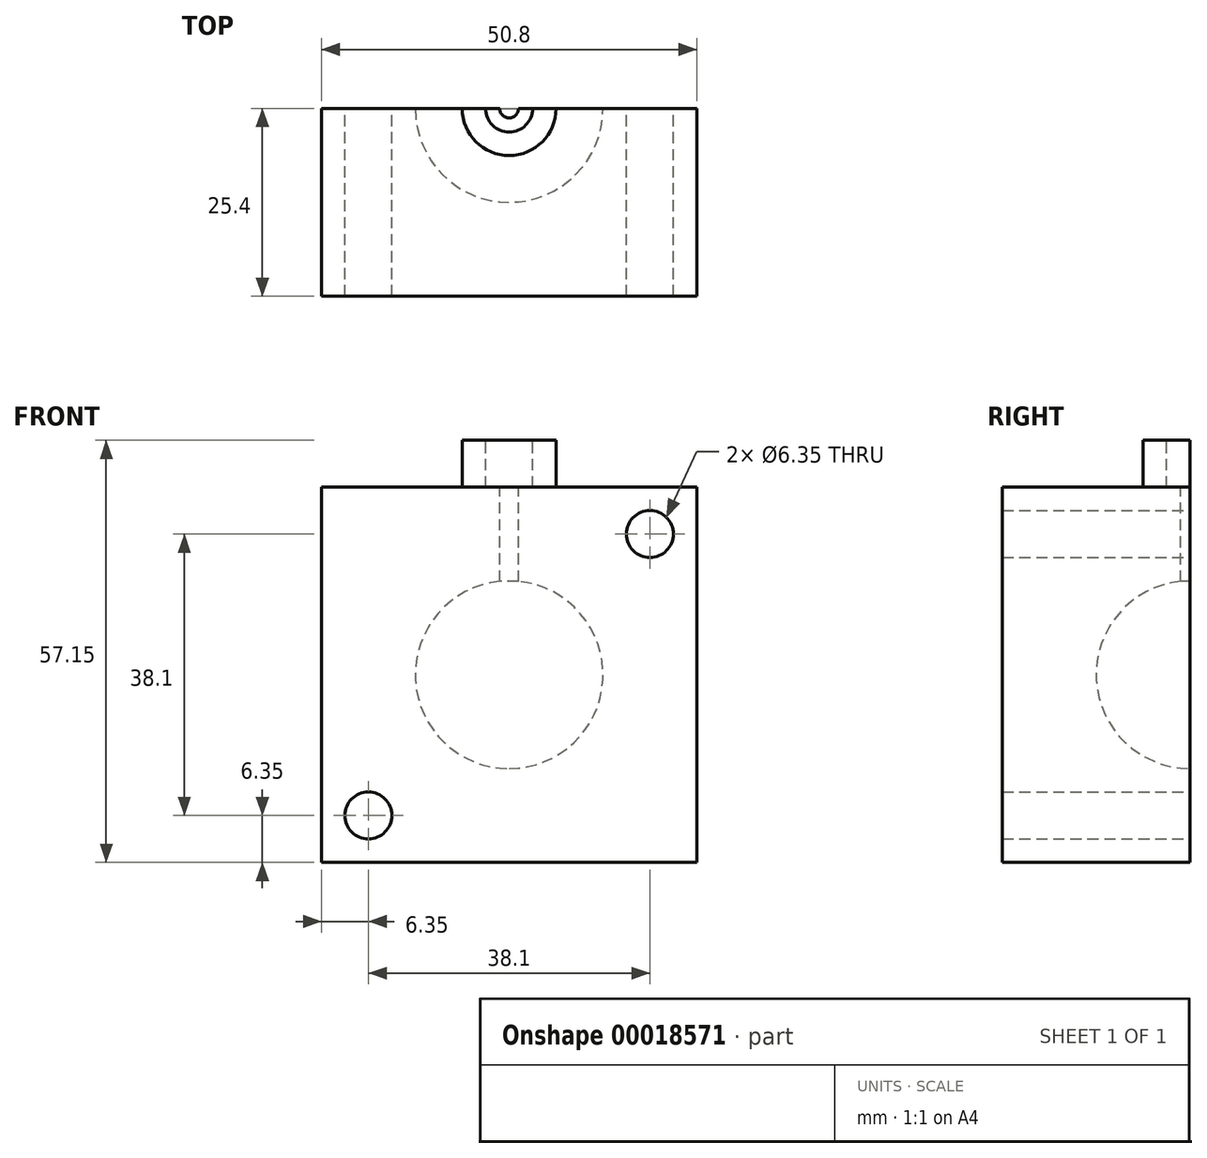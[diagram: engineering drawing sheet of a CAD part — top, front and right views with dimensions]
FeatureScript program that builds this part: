
annotation { "Feature Type Name" : "Feature", "Feature Type Description" : "" }
export const myFeature = defineFeature(function(context is Context, id is Id, definition is map)
    precondition{}
    {
        {
            var Q0;
            Q0=qCreatedBy(makeId("Front.planeOp"),FACE);
            var sketch = newSketch(context, id + "F0", { "sketchPlane" : qUnion([Q0])});
            skLineSegment(sketch, "E0.bottom", {"start": v(0, 0) * mm, "end": v(50.8, 0) * mm});
            skLineSegment(sketch, "E0.top", {"start": v(0, 50.8) * mm, "end": v(50.8, 50.8) * mm});
            skLineSegment(sketch, "E0.left", {"start": v(0, 0) * mm, "end": v(0, 50.8) * mm});
            skLineSegment(sketch, "E0.right", {"start": v(50.8, 0) * mm, "end": v(50.8, 50.8) * mm});
            skSolve(sketch);
        }
        {
            var Q0;
            Q0 = qSketchRegion(id + "F0", true);
            extrude(context, id + "F1", {"entities" : qUnion([Q0]), "depth" : 25.4 * mm});
        }
        {
            var Q0;
            Q0=makeQuery(id+"F1.opExtrude","CAP_FACE",FACE,{"disambiguationData":[OSD([sQuery(id+"F0.wireOp",EDGE,"E0.bottom"),sQuery(id+"F0.wireOp",EDGE,"E0.top"),sQuery(id+"F0.wireOp",EDGE,"E0.left"),sQuery(id+"F0.wireOp",EDGE,"E0.right")])],"isStart":true});
            var sketch = newSketch(context, id + "F11", { "sketchPlane" : qUnion([Q0])});
            skLineSegment(sketch, "E1", {"start": v(-25.4, 50.8) * mm, "end": v(-25.4, 0) * mm});
            skArc(sketch, "E2", {"start": v(-25.4, 12.7) * mm, "mid": v(-12.7, 25.4) * mm, "end": v(-25.4, 38.1) * mm});
            skSolve(sketch);
        }
        {
            var Q0;
            Q0 = qSketchRegion(id + "F11", true);
            var Q1;
            Q1=sQuery(id+"F11.wireOp",EDGE,"E1");
            revolve(context, id + "F2", {"operationType" : NewBodyOperationType.REMOVE, "entities" : qUnion([Q0]), "axis" : qUnion([Q1]), "revolveType" : RevolveType.FULL, "oppositeDirection" : true});
        }
        {
            var Q0;
            Q0=makeQuery(id+"F1.opExtrude","CAP_FACE",FACE,{"disambiguationData":[OSD([sQuery(id+"F0.wireOp",EDGE,"E0.bottom"),sQuery(id+"F0.wireOp",EDGE,"E0.top"),sQuery(id+"F0.wireOp",EDGE,"E0.left"),sQuery(id+"F0.wireOp",EDGE,"E0.right")])],"isStart":true});
            var sketch = newSketch(context, id + "F3", { "sketchPlane" : qUnion([Q0])});
            skLineSegment(sketch, "E3", {"start": v(0, 0) * mm, "end": v(0, 6.35) * mm});
            skLineSegment(sketch, "E4", {"start": v(0, 0) * mm, "end": v(-6.35, 0) * mm});
            skCircle(sketch, "E5", {"center": v(-6.35, 6.35) * mm, "radius": 3.18 * mm});
            skSolve(sketch);
        }
        {
            var Q0;
            Q0 = qSketchRegion(id + "F3", true);
            extrude(context, id + "F12", {"entities" : qUnion([Q0]), "operationType" : NewBodyOperationType.REMOVE, "endBound" : BoundingType.THROUGH_ALL, "oppositeDirection" : true, "depth" : 25.4 * mm});
        }
        {
            var Q0;
            Q0=makeQuery(id+"F1.opExtrude","CAP_FACE",FACE,{"disambiguationData":[OSD([sQuery(id+"F0.wireOp",EDGE,"E0.bottom"),sQuery(id+"F0.wireOp",EDGE,"E0.top"),sQuery(id+"F0.wireOp",EDGE,"E0.left"),sQuery(id+"F0.wireOp",EDGE,"E0.right")])],"isStart":true});
            var sketch = newSketch(context, id + "F4", { "sketchPlane" : qUnion([Q0])});
            skLineSegment(sketch, "E6", {"start": v(-50.8, 50.8) * mm, "end": v(-50.8, 44.45) * mm});
            skLineSegment(sketch, "E7", {"start": v(-50.8, 50.8) * mm, "end": v(-44.45, 50.8) * mm});
            skCircle(sketch, "E8", {"center": v(-44.45, 44.45) * mm, "radius": 3.18 * mm});
            skSolve(sketch);
        }
        {
            var Q0;
            Q0 = qSketchRegion(id + "F4", true);
            extrude(context, id + "F5", {"entities" : qUnion([Q0]), "operationType" : NewBodyOperationType.REMOVE, "endBound" : BoundingType.THROUGH_ALL, "oppositeDirection" : true, "depth" : 25.4 * mm});
        }
        {
            var Q0;
            Q0=makeQuery(id+"F1.opExtrude","SWEPT_FACE",FACE,{"disambiguationData":[OSD([sQuery(id+"F0.wireOp",EDGE,"E0.top")])]});
            var sketch = newSketch(context, id + "F6", { "sketchPlane" : qUnion([Q0])});
            skArc(sketch, "E9", {"start": v(19.05, 0) * mm, "mid": v(25.4, -6.35) * mm, "end": v(31.75, 0) * mm});
            skPoint(sketch, "E10.orphan", {"position": v(0, 0) * mm});
            skPoint(sketch, "E11.trimOffspring.end.orphan", {"position": v(50.8, 0) * mm});
            skLineSegment(sketch, "E12", {"start": v(19.05, 0) * mm, "end": v(31.75, 0) * mm});
            skSolve(sketch);
        }
        {
            var Q0;
            Q0 = qSketchRegion(id + "F6", true);
            extrude(context, id + "F7", {"entities" : qUnion([Q0]), "operationType" : NewBodyOperationType.ADD, "depth" : 6.35 * mm});
        }
        {
            var Q0;
            Q0=makeQuery(id+"F7.opExtrude","CAP_FACE",FACE,{"disambiguationData":[OSD([sQuery(id+"F6.wireOp",EDGE,"E9"),sQuery(id+"F6.wireOp",EDGE,"E12")])],"isStart":false});
            var sketch = newSketch(context, id + "F13", { "sketchPlane" : qUnion([Q0])});
            skLineSegment(sketch, "E13", {"start": v(31.75, 0) * mm, "end": v(19.05, 0) * mm});
            skCircle(sketch, "E14", {"center": v(25.4, 0) * mm, "radius": 3.18 * mm});
            skSolve(sketch);
        }
        {
            var Q0;
            Q0 = qSketchRegion(id + "F13", true);
            extrude(context, id + "F8", {"entities" : qUnion([Q0]), "operationType" : NewBodyOperationType.REMOVE, "oppositeDirection" : true, "depth" : 6.35 * mm});
        }
        {
            var Q0;
            Q0=makeQuery(id+"F8.boolean.opBoolean","COPY",FACE,{"derivedFrom":makeQuery(id+"F8.opExtrude","CAP_FACE",FACE,{"disambiguationData":[OSD([sQuery(id+"F13.wireOp",EDGE,"E14")])],"isStart":false})});
            var sketch = newSketch(context, id + "F9", { "sketchPlane" : qUnion([Q0])});
            skCircle(sketch, "E15", {"center": v(25.4, 0) * mm, "radius": 1.27 * mm});
            skSolve(sketch);
        }
        {
            var Q0;
            Q0 = qSketchRegion(id + "F9", true);
            extrude(context, id + "F10", {"entities" : qUnion([Q0]), "operationType" : NewBodyOperationType.REMOVE, "oppositeDirection" : true, "depth" : 25.4 * mm});
        }
    });
